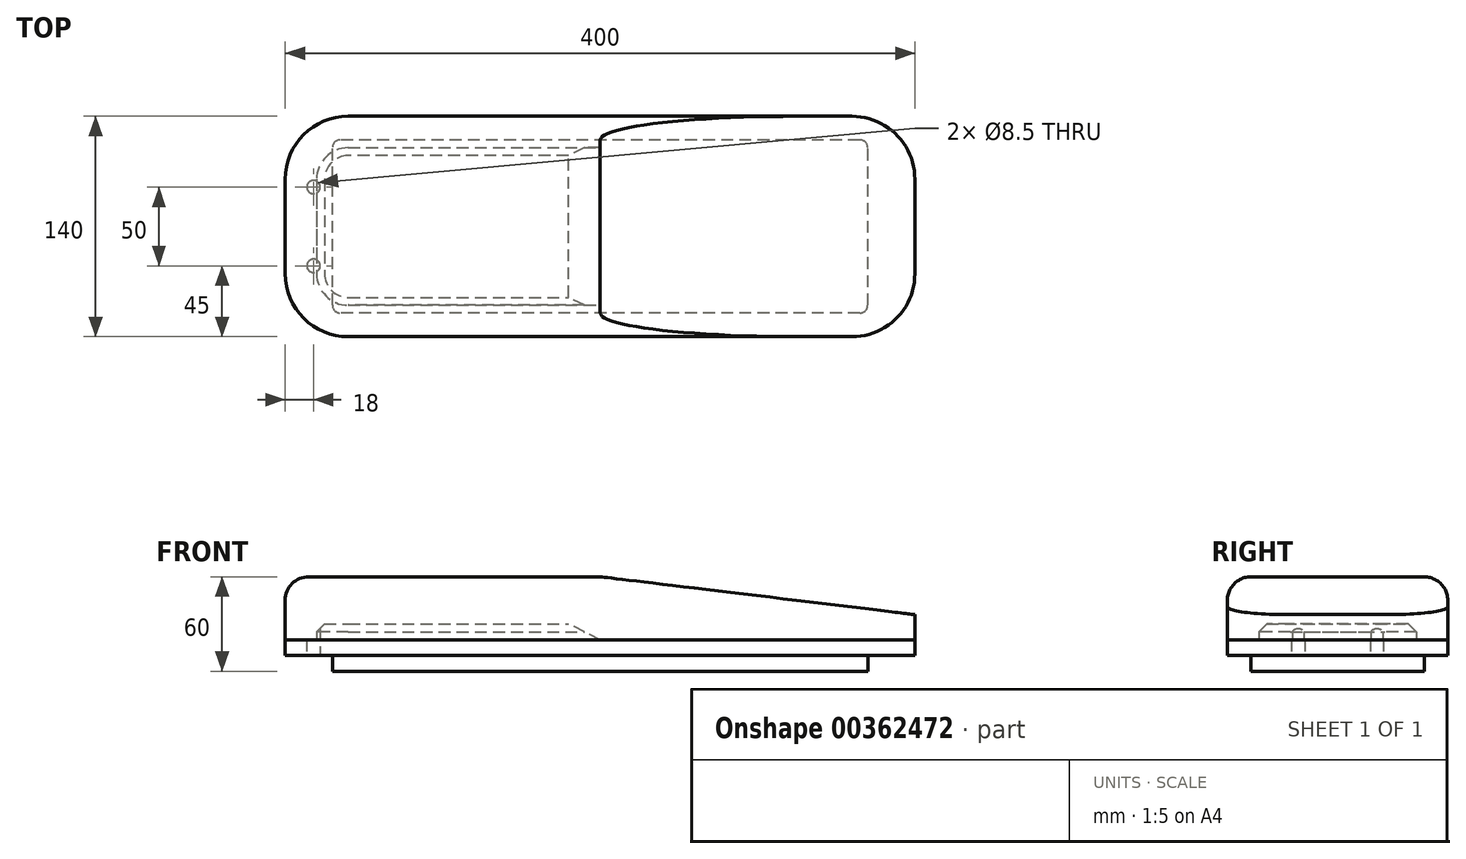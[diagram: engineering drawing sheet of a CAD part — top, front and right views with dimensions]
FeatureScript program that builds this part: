
annotation { "Feature Type Name" : "Feature", "Feature Type Description" : "" }
export const myFeature = defineFeature(function(context is Context, id is Id, definition is map)
    precondition{}
    {
        {
            var Q0;
            Q0=qCreatedBy(makeId("Top.planeOp"),FACE);
            var sketch = newSketch(context, id + "F0", { "sketchPlane" : qUnion([Q0])});
            skLineSegment(sketch, "E0.bottom", {"start": v(160, 70) * mm, "end": v(-160, 70) * mm});
            skLineSegment(sketch, "E0.top", {"start": v(160, -70) * mm, "end": v(-160, -70) * mm});
            skLineSegment(sketch, "E0.left", {"start": v(200, 30) * mm, "end": v(200, -30) * mm});
            skLineSegment(sketch, "E0.right", {"start": v(-200, 30) * mm, "end": v(-200, -30) * mm});
            skPoint(sketch, "E0.middle", {"position": v(0, 0) * mm});
            skPoint(sketch, "E1.visualSharp", {"position": v(-200, 70) * mm});
            skArc(sketch, "E1.filletArc", {"start": v(-160, 70) * mm, "mid": v(-188.28, 58.28) * mm, "end": v(-200, 30) * mm});
            skPoint(sketch, "E2.visualSharp", {"position": v(200, 70) * mm});
            skArc(sketch, "E2.filletArc", {"start": v(200, 30) * mm, "mid": v(188.28, 58.28) * mm, "end": v(160, 70) * mm});
            skPoint(sketch, "E3.visualSharp", {"position": v(200, -70) * mm});
            skArc(sketch, "E3.filletArc", {"start": v(160, -70) * mm, "mid": v(188.28, -58.28) * mm, "end": v(200, -30) * mm});
            skPoint(sketch, "E4.visualSharp", {"position": v(-200, -70) * mm});
            skArc(sketch, "E4.filletArc", {"start": v(-200, -30) * mm, "mid": v(-188.28, -58.28) * mm, "end": v(-160, -70) * mm});
            skSolve(sketch);
        }
        {
            var Q0;
            Q0 = qSketchRegion(id + "F0", true);
            extrude(context, id + "F1", {"entities" : qUnion([Q0]), "depth" : 10 * mm, "offsetDistance" : 25 * mm});
        }
        {
            var Q0;
            Q0=makeQuery(id+"F1.opExtrude","CAP_FACE",FACE,{"disambiguationData":[OSD([sQuery(id+"F0.wireOp",EDGE,"E0.bottom"),sQuery(id+"F0.wireOp",EDGE,"E0.top"),sQuery(id+"F0.wireOp",EDGE,"E0.left"),sQuery(id+"F0.wireOp",EDGE,"E0.right"),sQuery(id+"F0.wireOp",EDGE,"E1.filletArc"),sQuery(id+"F0.wireOp",EDGE,"E2.filletArc"),sQuery(id+"F0.wireOp",EDGE,"E3.filletArc"),sQuery(id+"F0.wireOp",EDGE,"E4.filletArc")])],"isStart":false});
            var sketch = newSketch(context, id + "F2", { "sketchPlane" : qUnion([Q0])});
            skLineSegment(sketch, "E5.bottom", {"start": v(-160, 50) * mm, "end": v(0, 50) * mm});
            skLineSegment(sketch, "E5.top", {"start": v(-160, -50) * mm, "end": v(0, -50) * mm});
            skLineSegment(sketch, "E5.left", {"start": v(-180, 30) * mm, "end": v(-180, -30) * mm});
            skLineSegment(sketch, "E5.right", {"start": v(0, 50) * mm, "end": v(0, -50) * mm});
            skPoint(sketch, "E6.visualSharp", {"position": v(-160, 30) * mm});
            skArc(sketch, "E6.filletArc", {"start": v(-160, 50) * mm, "mid": v(-174.14, 44.14) * mm, "end": v(-180, 30) * mm});
            skPoint(sketch, "E7.visualSharp", {"position": v(-180, -50) * mm});
            skArc(sketch, "E7.filletArc", {"start": v(-180, -30) * mm, "mid": v(-174.14, -44.14) * mm, "end": v(-160, -50) * mm});
            skSolve(sketch);
        }
        {
            var Q0;
            Q0 = qSketchRegion(id + "F2", true);
            extrude(context, id + "F3", {"entities" : qUnion([Q0]), "operationType" : NewBodyOperationType.ADD, "depth" : 10 * mm, "offsetDistance" : 25 * mm});
        }
        {
            var Q0;
            Q0=makeQuery(id+"F3.opExtrude","CAP_EDGE",EDGE,{"disambiguationData":[OSD([sQuery(id+"F2.wireOp",EDGE,"E5.right")])],"isStart":false});
            chamfer(context, id + "F4", {"entities" : qUnion([Q0]), "chamferType" : ChamferType.TWO_OFFSETS, "width1" : 10 * mm, "oppositeDirection" : false, "width2" : 20 * mm, "tangentPropagation" : true});
        }
        {
            var Q0;
            Q0=makeQuery(id+"F3.opExtrude","CAP_EDGE",EDGE,{"disambiguationData":[OSD([sQuery(id+"F2.wireOp",EDGE,"E5.top")])],"isStart":false});
            var Q1;
            Q1=makeQuery(id+"F3.opExtrude","CAP_EDGE",EDGE,{"disambiguationData":[OSD([sQuery(id+"F2.wireOp",EDGE,"E7.filletArc")])],"isStart":false});
            chamfer(context, id + "F5", {"entities" : qUnion([Q0, Q1]), "width" : 5 * mm, "tangentPropagation" : true});
        }
        {
            var Q0;
            Q0=makeQuery(id+"F1.opExtrude","CAP_FACE",FACE,{"disambiguationData":[OSD([sQuery(id+"F0.wireOp",EDGE,"E0.bottom"),sQuery(id+"F0.wireOp",EDGE,"E0.top"),sQuery(id+"F0.wireOp",EDGE,"E0.left"),sQuery(id+"F0.wireOp",EDGE,"E0.right"),sQuery(id+"F0.wireOp",EDGE,"E1.filletArc"),sQuery(id+"F0.wireOp",EDGE,"E2.filletArc"),sQuery(id+"F0.wireOp",EDGE,"E3.filletArc"),sQuery(id+"F0.wireOp",EDGE,"E4.filletArc")])],"isStart":true});
            var sketch = newSketch(context, id + "F6", { "sketchPlane" : qUnion([Q0])});
            skLineSegment(sketch, "E8.bottom", {"start": v(165, 55) * mm, "end": v(-165, 55) * mm});
            skLineSegment(sketch, "E8.top", {"start": v(165, -55) * mm, "end": v(-165, -55) * mm});
            skLineSegment(sketch, "E8.left", {"start": v(170, 50) * mm, "end": v(170, -50) * mm});
            skLineSegment(sketch, "E8.right", {"start": v(-170, 50) * mm, "end": v(-170, -50) * mm});
            skPoint(sketch, "E8.middle", {"position": v(0, 0) * mm});
            skPoint(sketch, "E9.visualSharp", {"position": v(-170, 55) * mm});
            skArc(sketch, "E9.filletArc", {"start": v(-165, 55) * mm, "mid": v(-168.54, 53.54) * mm, "end": v(-170, 50) * mm});
            skPoint(sketch, "E10.visualSharp", {"position": v(170, 55) * mm});
            skArc(sketch, "E10.filletArc", {"start": v(170, 50) * mm, "mid": v(168.54, 53.54) * mm, "end": v(165, 55) * mm});
            skPoint(sketch, "E11.visualSharp", {"position": v(170, -55) * mm});
            skArc(sketch, "E11.filletArc", {"start": v(165, -55) * mm, "mid": v(168.54, -53.54) * mm, "end": v(170, -50) * mm});
            skPoint(sketch, "E12.visualSharp", {"position": v(-170, -55) * mm});
            skArc(sketch, "E12.filletArc", {"start": v(-170, -50) * mm, "mid": v(-168.54, -53.54) * mm, "end": v(-165, -55) * mm});
            skSolve(sketch);
        }
        {
            var Q0;
            Q0 = qSketchRegion(id + "F6", true);
            extrude(context, id + "F7", {"entities" : qUnion([Q0]), "operationType" : NewBodyOperationType.ADD, "depth" : 10 * mm, "offsetDistance" : 25 * mm});
        }
        {
            var Q0;
            Q0=makeQuery(id+"F1.opExtrude","CAP_FACE",FACE,{"disambiguationData":[OSD([sQuery(id+"F0.wireOp",EDGE,"E0.bottom"),sQuery(id+"F0.wireOp",EDGE,"E0.top"),sQuery(id+"F0.wireOp",EDGE,"E0.left"),sQuery(id+"F0.wireOp",EDGE,"E0.right"),sQuery(id+"F0.wireOp",EDGE,"E1.filletArc"),sQuery(id+"F0.wireOp",EDGE,"E2.filletArc"),sQuery(id+"F0.wireOp",EDGE,"E3.filletArc"),sQuery(id+"F0.wireOp",EDGE,"E4.filletArc")])],"isStart":false});
            var sketch = newSketch(context, id + "F8", { "sketchPlane" : qUnion([Q0])});
            skLineSegment(sketch, "E13.0", {"start": v(160, 70) * mm, "end": v(-160, 70) * mm});
            skArc(sketch, "E14.0", {"start": v(-160, 70) * mm, "mid": v(-188.28, 58.28) * mm, "end": v(-200, 30) * mm});
            skLineSegment(sketch, "E15.0", {"start": v(-200, 30) * mm, "end": v(-200, -30) * mm});
            skArc(sketch, "E16.0", {"start": v(-200, -30) * mm, "mid": v(-188.28, -58.28) * mm, "end": v(-160, -70) * mm});
            skLineSegment(sketch, "E17.0", {"start": v(160, -70) * mm, "end": v(-160, -70) * mm});
            skArc(sketch, "E18.0", {"start": v(160, -70) * mm, "mid": v(188.28, -58.28) * mm, "end": v(200, -30) * mm});
            skLineSegment(sketch, "E19.0", {"start": v(200, 30) * mm, "end": v(200, -30) * mm});
            skArc(sketch, "E20.0", {"start": v(200, 30) * mm, "mid": v(188.28, 58.28) * mm, "end": v(160, 70) * mm});
            skSolve(sketch);
        }
        {
            var Q0;
            Q0 = qSketchRegion(id + "F8", true);
            extrude(context, id + "F9", {"entities" : qUnion([Q0]), "depth" : 40 * mm, "offsetDistance" : 25 * mm});
        }
        {
            var Q0;
            Q0=makeQuery(id+"F9.opExtrude","SWEPT_FACE",FACE,{"disambiguationData":[OSD([sQuery(id+"F8.wireOp",EDGE,"E17.0")])]});
            var sketch = newSketch(context, id + "F10", { "sketchPlane" : qUnion([Q0])});
            skLineSegment(sketch, "E21", {"start": v(0, 50) * mm, "end": v(200, 25.95) * mm});
            skLineSegment(sketch, "E22", {"start": v(200, 25.95) * mm, "end": v(200, 50) * mm});
            skLineSegment(sketch, "E23", {"start": v(200, 50) * mm, "end": v(0, 50) * mm});
            skSolve(sketch);
        }
        {
            var Q0;
            Q0 = qSketchRegion(id + "F10", true);
            extrude(context, id + "F11", {"entities" : qUnion([Q0]), "operationType" : NewBodyOperationType.REMOVE, "endBound" : BoundingType.THROUGH_ALL, "oppositeDirection" : true, "depth" : 25 * mm, "offsetDistance" : 25 * mm});
        }
        {
            var Q0;
            Q0=makeQuery(id+"F9.opExtrude","CAP_EDGE",EDGE,{"disambiguationData":[OSD([sQuery(id+"F8.wireOp",EDGE,"E17.0")])],"isStart":false});
            var Q1;
            Q1=makeQuery(id+"F11.boolean.opBoolean","COPY",EDGE,{"derivedFrom":makeQuery(id+"F11.opExtrude","CAP_EDGE",EDGE,{"disambiguationData":[OSD([sQuery(id+"F10.wireOp",EDGE,"E21")])],"isStart":true})});
            fillet(context, id + "F12", {"entities" : qUnion([Q0, Q1]), "radius" : 15 * mm, "tangentPropagation" : true, "allowEdgeOverflow" : false});
        }
        {
            var Q0;
            Q0=makeQuery(id+"F1.opExtrude","SWEPT_BODY",BODY,{"disambiguationData":[OSD([sQuery(id+"F0.wireOp",EDGE,"E0.bottom"),sQuery(id+"F0.wireOp",EDGE,"E0.top"),sQuery(id+"F0.wireOp",EDGE,"E0.left"),sQuery(id+"F0.wireOp",EDGE,"E0.right"),sQuery(id+"F0.wireOp",EDGE,"E1.filletArc"),sQuery(id+"F0.wireOp",EDGE,"E2.filletArc"),sQuery(id+"F0.wireOp",EDGE,"E3.filletArc"),sQuery(id+"F0.wireOp",EDGE,"E4.filletArc")])]});
            var Q1;
            Q1=makeQuery(id+"F9.opExtrude","SWEPT_BODY",BODY,{"disambiguationData":[OSD([sQuery(id+"F8.wireOp",EDGE,"E13.0"),sQuery(id+"F8.wireOp",EDGE,"E14.0"),sQuery(id+"F8.wireOp",EDGE,"E15.0"),sQuery(id+"F8.wireOp",EDGE,"E16.0"),sQuery(id+"F8.wireOp",EDGE,"E17.0"),sQuery(id+"F8.wireOp",EDGE,"E18.0"),sQuery(id+"F8.wireOp",EDGE,"E19.0"),sQuery(id+"F8.wireOp",EDGE,"E20.0")])]});
            booleanBodies(context, id + "F13", {"operationType" : BooleanOperationType.SUBTRACTION, "tools" : qUnion([Q0]), "targets" : qUnion([Q1]), "keepTools" : true});
        }
        {
            var Q0;
            Q0=makeQuery(id+"F1.opExtrude","CAP_FACE",FACE,{"disambiguationData":[OSD([sQuery(id+"F0.wireOp",EDGE,"E0.bottom"),sQuery(id+"F0.wireOp",EDGE,"E0.top"),sQuery(id+"F0.wireOp",EDGE,"E0.left"),sQuery(id+"F0.wireOp",EDGE,"E0.right"),sQuery(id+"F0.wireOp",EDGE,"E1.filletArc"),sQuery(id+"F0.wireOp",EDGE,"E2.filletArc"),sQuery(id+"F0.wireOp",EDGE,"E3.filletArc"),sQuery(id+"F0.wireOp",EDGE,"E4.filletArc")])],"isStart":true});
            var sketch = newSketch(context, id + "F14", { "sketchPlane" : qUnion([Q0])});
            skLineSegment(sketch, "E24", {"start": v(-200, 0) * mm, "end": v(-170, 0) * mm, "construction": true});
            skCircle(sketch, "E25", {"center": v(-182, 25) * mm, "radius": 4.25 * mm});
            skCircle(sketch, "E26.MirrorC", {"center": v(-182, -25) * mm, "radius": 4.25 * mm});
            skSolve(sketch);
        }
        {
            var Q0;
            Q0 = qSketchRegion(id + "F14", true);
            extrude(context, id + "F15", {"entities" : qUnion([Q0]), "operationType" : NewBodyOperationType.REMOVE, "endBound" : BoundingType.UP_TO_NEXT, "oppositeDirection" : true, "depth" : 25 * mm, "offsetDistance" : 25 * mm});
        }
    });
